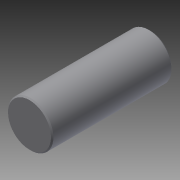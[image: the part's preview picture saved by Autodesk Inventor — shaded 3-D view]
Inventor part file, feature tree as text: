
AUTODESK INVENTOR PART (.ipt)
format: ipt  version: 2014 SP2 (Build 180246200, 246)  size: 102,912 bytes
history: native  units: in
note: dims shown in document units (in); Inventor stores cm internally (conversion verified against a paired STEP export)
features: other x35, revolve x1, sketch x1
ambient origin geometry x8: Origin, YZ Plane, XZ Plane, XY Plane, X Axis, Y Axis, Z Axis, Center Point
bodies: Solid1 (feature_tree)
feature tree (37):
  revolve  "Revolution1"  [1 undecoded]
  other  "dia1_XY"
  other  "dia1_YZ"
  other  "dia1_ZX"
  other  "dia1_X"
  other  "dia1_Y"
  other  "dia1_Z"
  other  "dia1_Center"
  other  "dia2_XY"
  other  "dia2_YZ"
  other  "dia2_ZX"
  other  "dia2_X"
  other  "dia2_Y"
  other  "dia2_Z"
  other  "dia2_Center"
  other  "pin_XY"
  other  "pin_YZ"
  other  "pin_ZX"
  other  "pin_X"
  other  "pin_Y"
  other  "pin_Z"
  other  "pin_Center"
  other  "pin1_XY"
  other  "pin1_YZ"
  other  "pin1_ZX"
  other  "pin1_X"
  other  "pin1_Y"
  other  "pin1_Z"
  other  "pin1_Center"
  other  "pin2_XY"
  other  "pin2_YZ"
  other  "pin2_ZX"
  other  "pin2_X"
  other  "pin2_Y"
  other  "pin2_Z"
  other  "pin2_Center"
  sketch  "Sketch_1"  dims[d0=360.0deg]
note: 1 required parameter value undecoded (feature->parameter linkage not recoverable at this tier; creation-order binding heuristic only, values carry confidence <= 0.55)
